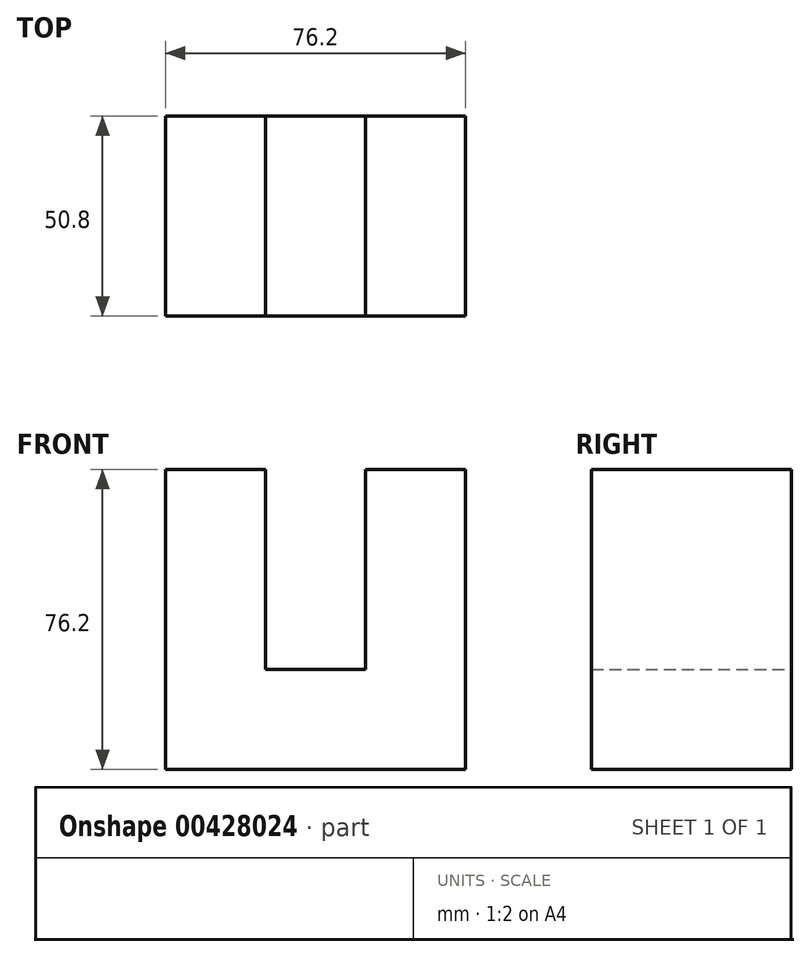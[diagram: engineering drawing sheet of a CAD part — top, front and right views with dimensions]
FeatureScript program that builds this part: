
annotation { "Feature Type Name" : "Feature", "Feature Type Description" : "" }
export const myFeature = defineFeature(function(context is Context, id is Id, definition is map)
    precondition{}
    {
        {
            var Q0;
            Q0=qCreatedBy(makeId("Front.planeOp"),FACE);
            var sketch = newSketch(context, id + "F0", { "sketchPlane" : qUnion([Q0])});
            skLineSegment(sketch, "E0", {"start": v(-76.2, 0) * mm, "end": v(-76.2, 76.2) * mm});
            skLineSegment(sketch, "E1", {"start": v(-76.2, 0) * mm, "end": v(0, 0) * mm});
            skLineSegment(sketch, "E2", {"start": v(-76.2, 76.2) * mm, "end": v(-50.8, 76.2) * mm});
            skLineSegment(sketch, "E3", {"start": v(-50.8, 76.2) * mm, "end": v(-50.8, 25.4) * mm});
            skLineSegment(sketch, "E4", {"start": v(-50.8, 25.4) * mm, "end": v(-25.4, 25.4) * mm});
            skLineSegment(sketch, "E5", {"start": v(-25.4, 25.4) * mm, "end": v(-25.4, 76.2) * mm});
            skLineSegment(sketch, "E6", {"start": v(-25.4, 76.2) * mm, "end": v(0, 76.2) * mm});
            skLineSegment(sketch, "E7", {"start": v(0, 76.2) * mm, "end": v(0, 0) * mm});
            skSolve(sketch);
        }
        {
            var Q0;
            Q0 = qSketchRegion(id + "F0", true);
            extrude(context, id + "F1", {"entities" : qUnion([Q0]), "depth" : 50.8 * mm});
        }
    });
